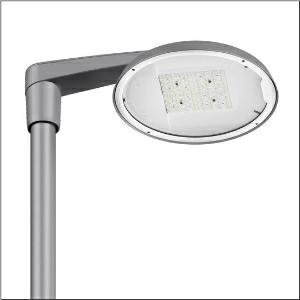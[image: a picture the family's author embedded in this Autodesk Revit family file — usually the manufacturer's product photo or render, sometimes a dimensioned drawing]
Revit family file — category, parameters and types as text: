
# Revit family: dl_r__50_iq_mini___st0_5a_5xa248b31f08me_0590
name_source: partatom
category: Lighting Fixtures
units: mm (PartAtom-declared; Revit-internal decimal feet)

## family parameters
Cut with Voids When Loaded = No
Host = Face
Light Source = No
Part Type = Normal
Room Calculation Point = No
Round Connector Dimension = Use Diameter
Shared = No

## types (1)
- --- (1 x LED, 15660 lm, 107.8 W, 3000K)
    Apparent Load = 108 VA
    CIE Flux Codes = 41 75 97 100 100
    Color Rendering = 70
    Color Temperature = 3000K
    Default Elevation = 1800 mm
    Description = DL® 50 iQ mini, mast luminaire, primary light control with lens, of PMMA, primary optical cover: cover, of toughened safety glass, transparent, light distribution: ST0.5a, light emission: direct distribution, primary light characteristic: asymmetric, installation type: side-entry, post-top, LED, High Power LED, rated luminous flux: 15.660lm, luminous efficacy: 145lm/W, light colour: 730, colour temperature: 3000K, control: optimised constant luminous flux control (CLO 2.0), Desk-Remote (wireless, voltage-free reading and setting of iQ features in the workshop via application-optimized NFC function/RFID function), Light-Fading, Smart-Wire, Night-Set, Lumen-Switch, Temp-Guard, Auto-Match, Street-Remote, mains connection: 230..240V, AC, 50/60Hz, connection cable pre-assembled, cable length: 10,5m, start of lifetime: 108W, end of service life: 118W, reduction: 47W, luminaire housing, of diecast aluminium, powder-coated, Siteco® metallic grey (DB 702S), inclination adjustable: 0°, 5°, 10° (post-top) | 0°, -5°, -10°, -15° (side-entry), please order mast post-top element or mast side-entry element separately, diameter: 500mm, height: 115mm, post-top: for spigot size d x l = 76 x 100mm; with reducer (optional accessory) 60 x 100mm | side-entry: for spigot size d x l = 60 x 100mm; with reducer (optional accessory) 42 x 100mm, protection rating (complete): IP66, insulation class (complete): insulation class II (safety insulation), certification: CE, ENEC, VDE, impact resistance: IK08, permissible operating ambient temperature for outdoor applications: -25..+40°C, standard-compliant lighting for roads and squares, packaging unit: 1 piece

Light Distribution: ST0.5a
    Height = 115 mm
    Lamp = 1 x LED
    Lamp Light Flux = 15660 lm
    Lamp Power = 107.8 W
    Lamp count = 1
    Length = 500 mm
    Luminous efficacy = 145 lm/W
    Manufacturer = Siteco
    ModVariant = No
    Model = 5XA248B31F08ME
    Number of Poles = 1
    OnlyDefault = Yes
    Power Factor = 1
    Product Name = DL® 50 iQ mini | ST0.5a
    Product group = mast luminaire | pylon top
    ProductGroupID = 6100
    Protection Class = Protection class II
    Protection Degree = IP 66
    RLX_Detail_Level = 1
    RLX_Emergency_Light_Flux = 0 lm
    RLX_Emergency_Type = 0
    RLX_Emergency_Type_DB = No
    RlxData = <blob elided: 127985 chars, md5=5281cbd8>
    Socket = socket
    Standby Power = 0 W
    System Light Flux = 15660 lm
    System Power = 108 W
    Type Comments = factory setting: luminous flux: 100 % | dim-lin: 254 | 565 mA
    Type Image = l_1251790.jpg
    URL = http://relux.com
    VarID = @adj_092441
    Voltage = 0 V
    Weight = 0.00 kg
    Width = 0 mm  [stored 0 ft]

note: [stored X ft] marks values corroborated as IEEE doubles in the binary element streams (Revit-internal decimal feet)

## geometry (parser evidence)
native form markers: Blend x4, Sweep x11
no freeform markers — native parametric forms only
